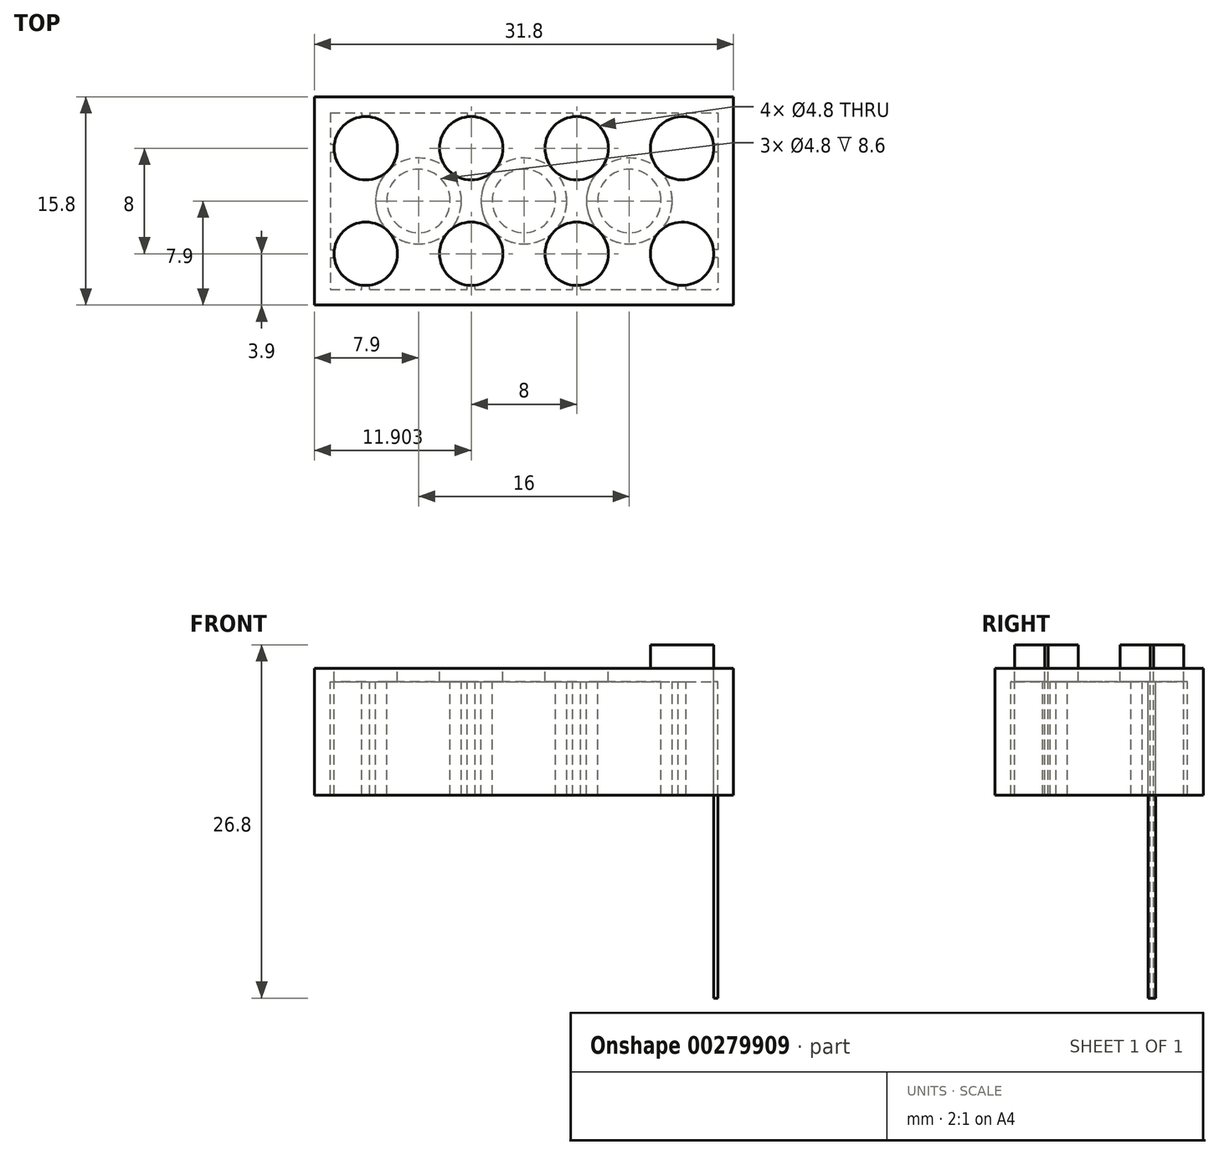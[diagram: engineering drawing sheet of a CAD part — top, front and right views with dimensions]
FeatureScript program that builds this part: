
annotation { "Feature Type Name" : "Feature", "Feature Type Description" : "" }
export const myFeature = defineFeature(function(context is Context, id is Id, definition is map)
    precondition{}
    {
        {
            var Q0;
            Q0=qCreatedBy(makeId("Top.planeOp"),FACE);
            var sketch = newSketch(context, id + "F0", { "sketchPlane" : qUnion([Q0])});
            skLineSegment(sketch, "E0.bottom", {"start": v(-15.9, 7.9) * mm, "end": v(15.9, 7.9) * mm});
            skLineSegment(sketch, "E0.top", {"start": v(-15.9, -7.9) * mm, "end": v(15.9, -7.9) * mm});
            skLineSegment(sketch, "E0.left", {"start": v(-15.9, 7.9) * mm, "end": v(-15.9, -7.9) * mm});
            skLineSegment(sketch, "E0.right", {"start": v(15.9, 7.9) * mm, "end": v(15.9, -7.9) * mm});
            skPoint(sketch, "E0.middle", {"position": v(0, 0) * mm});
            skCircle(sketch, "E1", {"center": v(0, 0) * mm, "radius": 3.25 * mm});
            skCircle(sketch, "E2", {"center": v(0, 0) * mm, "radius": 2.4 * mm});
            skLineSegment(sketch, "E3.bottom", {"start": v(-14.7, 6.7) * mm, "end": v(14.7, 6.7) * mm});
            skLineSegment(sketch, "E3.top", {"start": v(-14.7, -6.7) * mm, "end": v(14.7, -6.7) * mm});
            skLineSegment(sketch, "E3.left", {"start": v(-14.7, 6.7) * mm, "end": v(-14.7, -6.7) * mm});
            skLineSegment(sketch, "E3.right", {"start": v(14.7, 6.7) * mm, "end": v(14.7, -6.7) * mm});
            skCircle(sketch, "E4.1.0.0", {"center": v(8, 0) * mm, "radius": 3.25 * mm});
            skCircle(sketch, "E4.1.0.1", {"center": v(8, 0) * mm, "radius": 2.4 * mm});
            skLineSegment(sketch, "E4.direction1", {"start": v(0, 0) * mm, "end": v(8, 0) * mm, "construction": true});
            skCircle(sketch, "E5.1.0.0", {"center": v(-8, 0) * mm, "radius": 2.4 * mm});
            skCircle(sketch, "E5.1.0.1", {"center": v(-8, 0) * mm, "radius": 3.25 * mm});
            skLineSegment(sketch, "E5.direction1", {"start": v(0, 0) * mm, "end": v(-8, 0) * mm, "construction": true});
            skCircle(sketch, "E6", {"center": v(-12, 4) * mm, "radius": 2.4 * mm});
            skCircle(sketch, "E7.0.1.0", {"center": v(-12, -4) * mm, "radius": 2.4 * mm});
            skCircle(sketch, "E7.1.0.0", {"center": v(-4, 4) * mm, "radius": 2.4 * mm});
            skCircle(sketch, "E7.1.1.0", {"center": v(-4, -4) * mm, "radius": 2.4 * mm});
            skCircle(sketch, "E7.2.0.0", {"center": v(4, 4) * mm, "radius": 2.4 * mm});
            skCircle(sketch, "E7.2.1.0", {"center": v(4, -4) * mm, "radius": 2.4 * mm});
            skCircle(sketch, "E7.3.0.0", {"center": v(12, 4) * mm, "radius": 2.4 * mm});
            skCircle(sketch, "E7.3.1.0", {"center": v(12, -4) * mm, "radius": 2.4 * mm});
            skLineSegment(sketch, "E7.direction1", {"start": v(-12, 4) * mm, "end": v(-4, 4) * mm, "construction": true});
            skLineSegment(sketch, "E7.direction2", {"start": v(-12, 4) * mm, "end": v(-12, -4) * mm, "construction": true});
            skLineSegment(sketch, "E8.bottom", {"start": v(-12.3, 6.7) * mm, "end": v(-11.7, 6.7) * mm});
            skLineSegment(sketch, "E8.top", {"start": v(-12.3, 6.4) * mm, "end": v(-11.7, 6.4) * mm});
            skLineSegment(sketch, "E8.left", {"start": v(-12.3, 6.7) * mm, "end": v(-12.3, 6.4) * mm});
            skLineSegment(sketch, "E8.right", {"start": v(-11.7, 6.7) * mm, "end": v(-11.7, 6.4) * mm});
            skLineSegment(sketch, "E9.bottom", {"start": v(-14.7, 4.3) * mm, "end": v(-14.4, 4.3) * mm});
            skLineSegment(sketch, "E9.top", {"start": v(-14.7, 3.7) * mm, "end": v(-14.4, 3.7) * mm});
            skLineSegment(sketch, "E9.left", {"start": v(-14.7, 4.3) * mm, "end": v(-14.7, 3.7) * mm});
            skLineSegment(sketch, "E9.right", {"start": v(-14.4, 4.3) * mm, "end": v(-14.4, 3.7) * mm});
            skPoint(sketch, "E10", {"position": v(-12, 6.4) * mm});
            skPoint(sketch, "E11", {"position": v(-14.4, 4) * mm});
            skLineSegment(sketch, "E12.1.0.0", {"start": v(-4.3, 6.7) * mm, "end": v(-4.3, 6.4) * mm});
            skLineSegment(sketch, "E12.1.0.1", {"start": v(-4.3, 6.7) * mm, "end": v(-3.7, 6.7) * mm});
            skLineSegment(sketch, "E12.1.0.2", {"start": v(-3.7, 6.7) * mm, "end": v(-3.7, 6.4) * mm});
            skLineSegment(sketch, "E12.1.0.3", {"start": v(-4.3, 6.4) * mm, "end": v(-3.7, 6.4) * mm});
            skLineSegment(sketch, "E12.2.0.0", {"start": v(3.7, 6.7) * mm, "end": v(3.7, 6.4) * mm});
            skLineSegment(sketch, "E12.2.0.1", {"start": v(3.7, 6.7) * mm, "end": v(4.3, 6.7) * mm});
            skLineSegment(sketch, "E12.2.0.2", {"start": v(4.3, 6.7) * mm, "end": v(4.3, 6.4) * mm});
            skLineSegment(sketch, "E12.2.0.3", {"start": v(3.7, 6.4) * mm, "end": v(4.3, 6.4) * mm});
            skLineSegment(sketch, "E12.3.0.0", {"start": v(11.7, 6.7) * mm, "end": v(11.7, 6.4) * mm});
            skLineSegment(sketch, "E12.3.0.1", {"start": v(11.7, 6.7) * mm, "end": v(12.3, 6.7) * mm});
            skLineSegment(sketch, "E12.3.0.2", {"start": v(12.3, 6.7) * mm, "end": v(12.3, 6.4) * mm});
            skLineSegment(sketch, "E12.3.0.3", {"start": v(11.7, 6.4) * mm, "end": v(12.3, 6.4) * mm});
            skLineSegment(sketch, "E12.direction1", {"start": v(-12.3, 6.4) * mm, "end": v(-4.3, 6.4) * mm, "construction": true});
            skLineSegment(sketch, "E13.MirrorCS", {"start": v(14.7, 4.3) * mm, "end": v(14.4, 4.3) * mm});
            skLineSegment(sketch, "E14.MirrorCS", {"start": v(14.4, 4.3) * mm, "end": v(14.4, 3.7) * mm});
            skLineSegment(sketch, "E15.MirrorCS", {"start": v(14.7, 4.3) * mm, "end": v(14.7, 3.7) * mm});
            skLineSegment(sketch, "E16.MirrorCS", {"start": v(14.7, 3.7) * mm, "end": v(14.4, 3.7) * mm});
            skLineSegment(sketch, "E17.MirrorCS", {"start": v(-14.7, -4.3) * mm, "end": v(-14.4, -4.3) * mm});
            skLineSegment(sketch, "E18.MirrorCS", {"start": v(-14.7, -4.3) * mm, "end": v(-14.7, -3.7) * mm});
            skLineSegment(sketch, "E19.MirrorCS", {"start": v(-14.7, -3.7) * mm, "end": v(-14.4, -3.7) * mm});
            skLineSegment(sketch, "E20.MirrorCS", {"start": v(-14.4, -4.3) * mm, "end": v(-14.4, -3.7) * mm});
            skLineSegment(sketch, "E21.MirrorCS", {"start": v(-12.3, -6.7) * mm, "end": v(-12.3, -6.4) * mm});
            skLineSegment(sketch, "E22.MirrorCS", {"start": v(-12.3, -6.7) * mm, "end": v(-11.7, -6.7) * mm});
            skLineSegment(sketch, "E23.MirrorCS", {"start": v(-11.7, -6.7) * mm, "end": v(-11.7, -6.4) * mm});
            skLineSegment(sketch, "E24.MirrorCS", {"start": v(-12.3, -6.4) * mm, "end": v(-4.3, -6.4) * mm, "construction": true});
            skLineSegment(sketch, "E25.MirrorCS", {"start": v(-4.3, -6.7) * mm, "end": v(-4.3, -6.4) * mm});
            skLineSegment(sketch, "E26.MirrorCS", {"start": v(-4.3, -6.7) * mm, "end": v(-3.7, -6.7) * mm});
            skLineSegment(sketch, "E27.MirrorCS", {"start": v(-3.7, -6.7) * mm, "end": v(-3.7, -6.4) * mm});
            skLineSegment(sketch, "E28.MirrorCS", {"start": v(-4.3, -6.4) * mm, "end": v(-3.7, -6.4) * mm});
            skLineSegment(sketch, "E29.MirrorCS", {"start": v(3.7, -6.7) * mm, "end": v(3.7, -6.4) * mm});
            skLineSegment(sketch, "E30.MirrorCS", {"start": v(4.3, -6.7) * mm, "end": v(4.3, -6.4) * mm});
            skLineSegment(sketch, "E31.MirrorCS", {"start": v(3.7, -6.4) * mm, "end": v(4.3, -6.4) * mm});
            skLineSegment(sketch, "E32.MirrorCS", {"start": v(11.7, -6.7) * mm, "end": v(11.7, -6.4) * mm});
            skLineSegment(sketch, "E33.MirrorCS", {"start": v(11.7, -6.7) * mm, "end": v(12.3, -6.7) * mm});
            skLineSegment(sketch, "E34.MirrorCS", {"start": v(12.3, -6.7) * mm, "end": v(12.3, -6.4) * mm});
            skLineSegment(sketch, "E35.MirrorCS", {"start": v(11.7, -6.4) * mm, "end": v(12.3, -6.4) * mm});
            skLineSegment(sketch, "E36.MirrorCS", {"start": v(14.7, -4.3) * mm, "end": v(14.4, -4.3) * mm});
            skLineSegment(sketch, "E37.MirrorCS", {"start": v(14.7, -4.3) * mm, "end": v(14.7, -3.7) * mm});
            skLineSegment(sketch, "E38.MirrorCS", {"start": v(14.7, -3.7) * mm, "end": v(14.4, -3.7) * mm});
            skLineSegment(sketch, "E39.MirrorCS", {"start": v(14.4, -4.3) * mm, "end": v(14.4, -3.7) * mm});
            skLineSegment(sketch, "E40", {"start": v(-12.3, -6.4) * mm, "end": v(-11.7, -6.4) * mm});
            skSolve(sketch);
        }
        {
            var Q0;
            Q0=makeQuery(id+"F0.imprint","IMPRINT",FACE,{"disambiguationData":[TD([[makeQuery(id+"F0.imprint","IMPRINT",EDGE,{"derivedFrom":sQuery(id+"F0.wireOp",EDGE,"E0.bottom")}),-1.0]])]});
            extrude(context, id + "F1", {"entities" : qUnion([Q0]), "oppositeDirection" : true, "depth" : 9.6 * mm, "offsetDistance" : 25 * mm});
        }
        {
            var Q0;
            {var subQ0=sQuery(id+"F0.wireOp",EDGE,"E6");var subQ2=makeQuery(id+"F0.imprint","IMPRINT",VERTEX,{"derivedFrom":subQ0});Q0=makeQuery(id+"F0.imprint","IMPRINT",FACE,{"disambiguationData":[TD([[makeQuery(id+"F0.imprint","IMPRINT",EDGE,{"disambiguationData":[TD([[subQ2,-1.0]])],"derivedFrom":subQ0}),1.0]])]});}
            var Q1;
            {var subQ5=sQuery(id+"F0.wireOp",EDGE,"E8.left");Q1=makeQuery(id+"F0.imprint","IMPRINT",FACE,{"disambiguationData":[TD([[makeQuery(id+"F0.imprint","IMPRINT",EDGE,{"derivedFrom":subQ5}),-1.0]])]});}
            var Q2;
            Q2=makeQuery(id+"F0.imprint","IMPRINT",FACE,{"disambiguationData":[TD([[makeQuery(id+"F0.imprint","IMPRINT",EDGE,{"derivedFrom":sQuery(id+"F0.wireOp",EDGE,"E5.1.0.0")}),1.0]])]});
            var Q3;
            Q3=makeQuery(id+"F0.imprint","IMPRINT",FACE,{"disambiguationData":[TD([[makeQuery(id+"F0.imprint","IMPRINT",EDGE,{"derivedFrom":sQuery(id+"F0.wireOp",EDGE,"E5.1.0.0")}),-1.0]])]});
            var Q4;
            {var subQ0=sQuery(id+"F0.wireOp",EDGE,"E7.0.1.0");var subQ1=makeQuery(id+"F0.imprint","IMPRINT",VERTEX,{"derivedFrom":subQ0});Q4=makeQuery(id+"F0.imprint","IMPRINT",FACE,{"disambiguationData":[TD([[makeQuery(id+"F0.imprint","IMPRINT",EDGE,{"disambiguationData":[TD([[subQ1,-1.0]])],"derivedFrom":subQ0}),1.0]])]});}
            var Q5;
            {var subQ14=sQuery(id+"F0.wireOp",EDGE,"E8.right");Q5=makeQuery(id+"F0.imprint","IMPRINT",FACE,{"disambiguationData":[TD([[makeQuery(id+"F0.imprint","IMPRINT",EDGE,{"derivedFrom":subQ14}),1.0]])]});}
            var Q6;
            {var subQ0=sQuery(id+"F0.wireOp",EDGE,"E7.1.0.0");var subQ2=makeQuery(id+"F0.imprint","IMPRINT",VERTEX,{"derivedFrom":subQ0});Q6=makeQuery(id+"F0.imprint","IMPRINT",FACE,{"disambiguationData":[TD([[makeQuery(id+"F0.imprint","IMPRINT",EDGE,{"disambiguationData":[TD([[subQ2,-1.0]])],"derivedFrom":subQ0}),1.0]])]});}
            var Q7;
            {var subQ0=sQuery(id+"F0.wireOp",EDGE,"E7.1.1.0");var subQ1=makeQuery(id+"F0.imprint","IMPRINT",VERTEX,{"derivedFrom":subQ0});Q7=makeQuery(id+"F0.imprint","IMPRINT",FACE,{"disambiguationData":[TD([[makeQuery(id+"F0.imprint","IMPRINT",EDGE,{"disambiguationData":[TD([[subQ1,-1.0]])],"derivedFrom":subQ0}),1.0]])]});}
            var Q8;
            {var subQ10=sQuery(id+"F0.wireOp",EDGE,"E12.1.0.2");Q8=makeQuery(id+"F0.imprint","IMPRINT",FACE,{"disambiguationData":[TD([[makeQuery(id+"F0.imprint","IMPRINT",EDGE,{"derivedFrom":subQ10}),1.0]])]});}
            var Q9;
            {var subQ3=sQuery(id+"F0.wireOp",EDGE,"E25.MirrorCS");Q9=makeQuery(id+"F0.imprint","IMPRINT",FACE,{"disambiguationData":[TD([[makeQuery(id+"F0.imprint","IMPRINT",EDGE,{"derivedFrom":subQ3}),-1.0]])]});}
            var Q10;
            {var subQ3=sQuery(id+"F0.wireOp",EDGE,"E21.MirrorCS");Q10=makeQuery(id+"F0.imprint","IMPRINT",FACE,{"disambiguationData":[TD([[makeQuery(id+"F0.imprint","IMPRINT",EDGE,{"derivedFrom":subQ3}),-1.0]])]});}
            var Q11;
            {var subQ0=sQuery(id+"F0.wireOp",EDGE,"E17.MirrorCS");Q11=makeQuery(id+"F0.imprint","IMPRINT",FACE,{"disambiguationData":[TD([[makeQuery(id+"F0.imprint","IMPRINT",EDGE,{"derivedFrom":subQ0}),1.0]])]});}
            var Q12;
            {var subQ0=sQuery(id+"F0.wireOp",EDGE,"E8.left");Q12=makeQuery(id+"F0.imprint","IMPRINT",FACE,{"disambiguationData":[TD([[makeQuery(id+"F0.imprint","IMPRINT",EDGE,{"derivedFrom":subQ0}),1.0]])]});}
            var Q13;
            {var subQ2=sQuery(id+"F0.wireOp",EDGE,"E9.bottom");Q13=makeQuery(id+"F0.imprint","IMPRINT",FACE,{"disambiguationData":[TD([[makeQuery(id+"F0.imprint","IMPRINT",EDGE,{"derivedFrom":subQ2}),-1.0]])]});}
            var Q14;
            {var subQ3=sQuery(id+"F0.wireOp",EDGE,"E12.1.0.0");Q14=makeQuery(id+"F0.imprint","IMPRINT",FACE,{"disambiguationData":[TD([[makeQuery(id+"F0.imprint","IMPRINT",EDGE,{"derivedFrom":subQ3}),1.0]])]});}
            var Q15;
            Q15=makeQuery(id+"F0.imprint","IMPRINT",FACE,{"disambiguationData":[TD([[makeQuery(id+"F0.imprint","IMPRINT",EDGE,{"derivedFrom":sQuery(id+"F0.wireOp",EDGE,"E2")}),-1.0]])]});
            var Q16;
            Q16=makeQuery(id+"F0.imprint","IMPRINT",FACE,{"disambiguationData":[TD([[makeQuery(id+"F0.imprint","IMPRINT",EDGE,{"derivedFrom":sQuery(id+"F0.wireOp",EDGE,"E2")}),1.0]])]});
            var Q17;
            {var subQ0=sQuery(id+"F0.wireOp",EDGE,"E7.2.1.0");var subQ1=makeQuery(id+"F0.imprint","IMPRINT",VERTEX,{"derivedFrom":subQ0});Q17=makeQuery(id+"F0.imprint","IMPRINT",FACE,{"disambiguationData":[TD([[makeQuery(id+"F0.imprint","IMPRINT",EDGE,{"disambiguationData":[TD([[subQ1,-1.0]])],"derivedFrom":subQ0}),1.0]])]});}
            var Q18;
            {var subQ3=sQuery(id+"F0.wireOp",EDGE,"E29.MirrorCS");Q18=makeQuery(id+"F0.imprint","IMPRINT",FACE,{"disambiguationData":[TD([[makeQuery(id+"F0.imprint","IMPRINT",EDGE,{"derivedFrom":subQ3}),-1.0]])]});}
            var Q19;
            {var subQ16=sQuery(id+"F0.wireOp",EDGE,"E12.2.0.2");Q19=makeQuery(id+"F0.imprint","IMPRINT",FACE,{"disambiguationData":[TD([[makeQuery(id+"F0.imprint","IMPRINT",EDGE,{"derivedFrom":subQ16}),1.0]])]});}
            var Q20;
            {var subQ0=sQuery(id+"F0.wireOp",EDGE,"E7.3.1.0");var subQ1=makeQuery(id+"F0.imprint","INTERSECT",VERTEX,{"derivedFrom":[subQ0,sQuery(id+"F0.wireOp",EDGE,"E35.MirrorCS")]});Q20=makeQuery(id+"F0.imprint","IMPRINT",FACE,{"disambiguationData":[TD([[makeQuery(id+"F0.imprint","IMPRINT",EDGE,{"disambiguationData":[TD([[subQ1,1.0]])],"derivedFrom":subQ0}),1.0]])]});}
            var Q21;
            {var subQ0=sQuery(id+"F0.wireOp",EDGE,"E34.MirrorCS");Q21=makeQuery(id+"F0.imprint","IMPRINT",FACE,{"disambiguationData":[TD([[makeQuery(id+"F0.imprint","IMPRINT",EDGE,{"derivedFrom":subQ0}),-1.0]])]});}
            var Q22;
            {var subQ3=sQuery(id+"F0.wireOp",EDGE,"E32.MirrorCS");Q22=makeQuery(id+"F0.imprint","IMPRINT",FACE,{"disambiguationData":[TD([[makeQuery(id+"F0.imprint","IMPRINT",EDGE,{"derivedFrom":subQ3}),-1.0]])]});}
            var Q23;
            {var subQ0=sQuery(id+"F0.wireOp",EDGE,"E36.MirrorCS");Q23=makeQuery(id+"F0.imprint","IMPRINT",FACE,{"disambiguationData":[TD([[makeQuery(id+"F0.imprint","IMPRINT",EDGE,{"derivedFrom":subQ0}),-1.0]])]});}
            var Q24;
            Q24=makeQuery(id+"F0.imprint","IMPRINT",FACE,{"disambiguationData":[TD([[makeQuery(id+"F0.imprint","IMPRINT",EDGE,{"derivedFrom":sQuery(id+"F0.wireOp",EDGE,"E4.1.0.1")}),1.0]])]});
            var Q25;
            Q25=makeQuery(id+"F0.imprint","IMPRINT",FACE,{"disambiguationData":[TD([[makeQuery(id+"F0.imprint","IMPRINT",EDGE,{"derivedFrom":sQuery(id+"F0.wireOp",EDGE,"E4.1.0.1")}),-1.0]])]});
            var Q26;
            {var subQ0=sQuery(id+"F0.wireOp",EDGE,"E12.3.0.2");Q26=makeQuery(id+"F0.imprint","IMPRINT",FACE,{"disambiguationData":[TD([[makeQuery(id+"F0.imprint","IMPRINT",EDGE,{"derivedFrom":subQ0}),1.0]])]});}
            var Q27;
            {var subQ0=sQuery(id+"F0.wireOp",EDGE,"E13.MirrorCS");Q27=makeQuery(id+"F0.imprint","IMPRINT",FACE,{"disambiguationData":[TD([[makeQuery(id+"F0.imprint","IMPRINT",EDGE,{"derivedFrom":subQ0}),1.0]])]});}
            var Q28;
            {var subQ3=sQuery(id+"F0.wireOp",EDGE,"E12.3.0.0");Q28=makeQuery(id+"F0.imprint","IMPRINT",FACE,{"disambiguationData":[TD([[makeQuery(id+"F0.imprint","IMPRINT",EDGE,{"derivedFrom":subQ3}),1.0]])]});}
            var Q29;
            {var subQ0=sQuery(id+"F0.wireOp",EDGE,"E7.3.0.0");var subQ1=makeQuery(id+"F0.imprint","INTERSECT",VERTEX,{"derivedFrom":[subQ0,sQuery(id+"F0.wireOp",EDGE,"E12.3.0.3")]});Q29=makeQuery(id+"F0.imprint","IMPRINT",FACE,{"disambiguationData":[TD([[makeQuery(id+"F0.imprint","IMPRINT",EDGE,{"disambiguationData":[TD([[subQ1,1.0]])],"derivedFrom":subQ0}),1.0]])]});}
            var Q30;
            {var subQ0=sQuery(id+"F0.wireOp",EDGE,"E7.2.0.0");var subQ2=makeQuery(id+"F0.imprint","IMPRINT",VERTEX,{"derivedFrom":subQ0});Q30=makeQuery(id+"F0.imprint","IMPRINT",FACE,{"disambiguationData":[TD([[makeQuery(id+"F0.imprint","IMPRINT",EDGE,{"disambiguationData":[TD([[subQ2,-1.0]])],"derivedFrom":subQ0}),1.0]])]});}
            var Q31;
            {var subQ4=sQuery(id+"F0.wireOp",EDGE,"E12.2.0.0");Q31=makeQuery(id+"F0.imprint","IMPRINT",FACE,{"disambiguationData":[TD([[makeQuery(id+"F0.imprint","IMPRINT",EDGE,{"derivedFrom":subQ4}),1.0]])]});}
            extrude(context, id + "F2", {"entities" : qUnion([Q0, Q1, Q2, Q3, Q4, Q5, Q6, Q7, Q8, Q9, Q10, Q11, Q12, Q13, Q14, Q15, Q16, Q17, Q18, Q19, Q20, Q21, Q22, Q23, Q24, Q25, Q26, Q27, Q28, Q29, Q30, Q31]), "operationType" : NewBodyOperationType.ADD, "oppositeDirection" : true, "depth" : 1 * mm, "offsetDistance" : 25 * mm});
        }
        {
            var Q0;
            {var subQ0=sQuery(id+"F0.wireOp",EDGE,"E6");var subQ2=makeQuery(id+"F0.imprint","IMPRINT",VERTEX,{"derivedFrom":subQ0});Q0=makeQuery(id+"F0.imprint","IMPRINT",FACE,{"disambiguationData":[TD([[makeQuery(id+"F0.imprint","IMPRINT",EDGE,{"disambiguationData":[TD([[subQ2,-1.0]])],"derivedFrom":subQ0}),1.0]])]});}
            var Q1;
            {var subQ0=sQuery(id+"F0.wireOp",EDGE,"E7.1.0.0");var subQ2=makeQuery(id+"F0.imprint","IMPRINT",VERTEX,{"derivedFrom":subQ0});Q1=makeQuery(id+"F0.imprint","IMPRINT",FACE,{"disambiguationData":[TD([[makeQuery(id+"F0.imprint","IMPRINT",EDGE,{"disambiguationData":[TD([[subQ2,-1.0]])],"derivedFrom":subQ0}),1.0]])]});}
            var Q2;
            {var subQ0=sQuery(id+"F0.wireOp",EDGE,"E7.2.0.0");var subQ2=makeQuery(id+"F0.imprint","IMPRINT",VERTEX,{"derivedFrom":subQ0});Q2=makeQuery(id+"F0.imprint","IMPRINT",FACE,{"disambiguationData":[TD([[makeQuery(id+"F0.imprint","IMPRINT",EDGE,{"disambiguationData":[TD([[subQ2,-1.0]])],"derivedFrom":subQ0}),1.0]])]});}
            var Q3;
            {var subQ0=sQuery(id+"F0.wireOp",EDGE,"E7.3.0.0");var subQ1=makeQuery(id+"F0.imprint","INTERSECT",VERTEX,{"derivedFrom":[subQ0,sQuery(id+"F0.wireOp",EDGE,"E12.3.0.3")]});Q3=makeQuery(id+"F0.imprint","IMPRINT",FACE,{"disambiguationData":[TD([[makeQuery(id+"F0.imprint","IMPRINT",EDGE,{"disambiguationData":[TD([[subQ1,1.0]])],"derivedFrom":subQ0}),1.0]])]});}
            var Q4;
            {var subQ0=sQuery(id+"F0.wireOp",EDGE,"E7.3.1.0");var subQ1=makeQuery(id+"F0.imprint","INTERSECT",VERTEX,{"derivedFrom":[subQ0,sQuery(id+"F0.wireOp",EDGE,"E35.MirrorCS")]});Q4=makeQuery(id+"F0.imprint","IMPRINT",FACE,{"disambiguationData":[TD([[makeQuery(id+"F0.imprint","IMPRINT",EDGE,{"disambiguationData":[TD([[subQ1,1.0]])],"derivedFrom":subQ0}),1.0]])]});}
            var Q5;
            {var subQ0=sQuery(id+"F0.wireOp",EDGE,"E7.2.1.0");var subQ1=makeQuery(id+"F0.imprint","IMPRINT",VERTEX,{"derivedFrom":subQ0});Q5=makeQuery(id+"F0.imprint","IMPRINT",FACE,{"disambiguationData":[TD([[makeQuery(id+"F0.imprint","IMPRINT",EDGE,{"disambiguationData":[TD([[subQ1,-1.0]])],"derivedFrom":subQ0}),1.0]])]});}
            var Q6;
            {var subQ0=sQuery(id+"F0.wireOp",EDGE,"E7.1.1.0");var subQ1=makeQuery(id+"F0.imprint","IMPRINT",VERTEX,{"derivedFrom":subQ0});Q6=makeQuery(id+"F0.imprint","IMPRINT",FACE,{"disambiguationData":[TD([[makeQuery(id+"F0.imprint","IMPRINT",EDGE,{"disambiguationData":[TD([[subQ1,-1.0]])],"derivedFrom":subQ0}),1.0]])]});}
            var Q7;
            {var subQ0=sQuery(id+"F0.wireOp",EDGE,"E7.0.1.0");var subQ1=makeQuery(id+"F0.imprint","IMPRINT",VERTEX,{"derivedFrom":subQ0});Q7=makeQuery(id+"F0.imprint","IMPRINT",FACE,{"disambiguationData":[TD([[makeQuery(id+"F0.imprint","IMPRINT",EDGE,{"disambiguationData":[TD([[subQ1,-1.0]])],"derivedFrom":subQ0}),1.0]])]});}
            extrude(context, id + "F3", {"entities" : qUnion([Q0, Q1, Q2, Q3, Q4, Q5, Q6, Q7]), "operationType" : NewBodyOperationType.ADD, "depth" : 1.8 * mm, "offsetDistance" : 25 * mm});
        }
        {
            var Q0;
            {var subQ3=sQuery(id+"F0.wireOp",EDGE,"E32.MirrorCS");Q0=makeQuery(id+"F0.imprint","IMPRINT",FACE,{"disambiguationData":[TD([[makeQuery(id+"F0.imprint","IMPRINT",EDGE,{"derivedFrom":subQ3}),-1.0]])]});}
            var Q1;
            {var subQ3=sQuery(id+"F0.wireOp",EDGE,"E12.3.0.0");Q1=makeQuery(id+"F0.imprint","IMPRINT",FACE,{"disambiguationData":[TD([[makeQuery(id+"F0.imprint","IMPRINT",EDGE,{"derivedFrom":subQ3}),1.0]])]});}
            var Q2;
            {var subQ4=sQuery(id+"F0.wireOp",EDGE,"E12.2.0.0");Q2=makeQuery(id+"F0.imprint","IMPRINT",FACE,{"disambiguationData":[TD([[makeQuery(id+"F0.imprint","IMPRINT",EDGE,{"derivedFrom":subQ4}),1.0]])]});}
            var Q3;
            {var subQ3=sQuery(id+"F0.wireOp",EDGE,"E12.1.0.0");Q3=makeQuery(id+"F0.imprint","IMPRINT",FACE,{"disambiguationData":[TD([[makeQuery(id+"F0.imprint","IMPRINT",EDGE,{"derivedFrom":subQ3}),1.0]])]});}
            var Q4;
            {var subQ0=sQuery(id+"F0.wireOp",EDGE,"E8.left");Q4=makeQuery(id+"F0.imprint","IMPRINT",FACE,{"disambiguationData":[TD([[makeQuery(id+"F0.imprint","IMPRINT",EDGE,{"derivedFrom":subQ0}),1.0]])]});}
            var Q5;
            {var subQ2=sQuery(id+"F0.wireOp",EDGE,"E9.bottom");Q5=makeQuery(id+"F0.imprint","IMPRINT",FACE,{"disambiguationData":[TD([[makeQuery(id+"F0.imprint","IMPRINT",EDGE,{"derivedFrom":subQ2}),-1.0]])]});}
            var Q6;
            {var subQ0=sQuery(id+"F0.wireOp",EDGE,"E17.MirrorCS");Q6=makeQuery(id+"F0.imprint","IMPRINT",FACE,{"disambiguationData":[TD([[makeQuery(id+"F0.imprint","IMPRINT",EDGE,{"derivedFrom":subQ0}),1.0]])]});}
            var Q7;
            {var subQ3=sQuery(id+"F0.wireOp",EDGE,"E21.MirrorCS");Q7=makeQuery(id+"F0.imprint","IMPRINT",FACE,{"disambiguationData":[TD([[makeQuery(id+"F0.imprint","IMPRINT",EDGE,{"derivedFrom":subQ3}),-1.0]])]});}
            var Q8;
            {var subQ3=sQuery(id+"F0.wireOp",EDGE,"E25.MirrorCS");Q8=makeQuery(id+"F0.imprint","IMPRINT",FACE,{"disambiguationData":[TD([[makeQuery(id+"F0.imprint","IMPRINT",EDGE,{"derivedFrom":subQ3}),-1.0]])]});}
            var Q9;
            {var subQ3=sQuery(id+"F0.wireOp",EDGE,"E29.MirrorCS");Q9=makeQuery(id+"F0.imprint","IMPRINT",FACE,{"disambiguationData":[TD([[makeQuery(id+"F0.imprint","IMPRINT",EDGE,{"derivedFrom":subQ3}),-1.0]])]});}
            var Q10;
            Q10=makeQuery(id+"F0.imprint","IMPRINT",FACE,{"disambiguationData":[TD([[makeQuery(id+"F0.imprint","IMPRINT",EDGE,{"derivedFrom":sQuery(id+"F0.wireOp",EDGE,"E4.1.0.1")}),-1.0]])]});
            var Q11;
            Q11=makeQuery(id+"F0.imprint","IMPRINT",FACE,{"disambiguationData":[TD([[makeQuery(id+"F0.imprint","IMPRINT",EDGE,{"derivedFrom":sQuery(id+"F0.wireOp",EDGE,"E2")}),-1.0]])]});
            var Q12;
            Q12=makeQuery(id+"F0.imprint","IMPRINT",FACE,{"disambiguationData":[TD([[makeQuery(id+"F0.imprint","IMPRINT",EDGE,{"derivedFrom":sQuery(id+"F0.wireOp",EDGE,"E5.1.0.0")}),-1.0]])]});
            var Q13;
            {var subQ0=sQuery(id+"F0.wireOp",EDGE,"E36.MirrorCS");Q13=makeQuery(id+"F0.imprint","IMPRINT",FACE,{"disambiguationData":[TD([[makeQuery(id+"F0.imprint","IMPRINT",EDGE,{"derivedFrom":subQ0}),-1.0]])]});}
            extrude(context, id + "F4", {"entities" : qUnion([Q0, Q1, Q2, Q3, Q4, Q5, Q6, Q7, Q8, Q9, Q10, Q11, Q12, Q13]), "operationType" : NewBodyOperationType.ADD, "oppositeDirection" : true, "depth" : 9.6 * mm, "offsetDistance" : 25 * mm});
        }
        {
            var Q0;
            {var subQ0=sQuery(id+"F0.wireOp",EDGE,"E13.MirrorCS");Q0=makeQuery(id+"F0.imprint","IMPRINT",FACE,{"disambiguationData":[TD([[makeQuery(id+"F0.imprint","IMPRINT",EDGE,{"derivedFrom":subQ0}),1.0]])]});}
            extrude(context, id + "F5", {"entities" : qUnion([Q0]), "operationType" : NewBodyOperationType.ADD, "oppositeDirection" : true, "depth" : 25 * mm, "offsetDistance" : 25 * mm});
        }
        {
            var Q0;
            {var subQ0=sQuery(id+"F0.wireOp",EDGE,"E13.MirrorCS");Q0=makeQuery(id+"F0.imprint","IMPRINT",FACE,{"disambiguationData":[TD([[makeQuery(id+"F0.imprint","IMPRINT",EDGE,{"derivedFrom":subQ0}),1.0]])]});}
            extrude(context, id + "F6", {"entities" : qUnion([Q0]), "operationType" : NewBodyOperationType.ADD, "oppositeDirection" : true, "depth" : 9.6 * mm, "offsetDistance" : 25 * mm});
        }
    });
